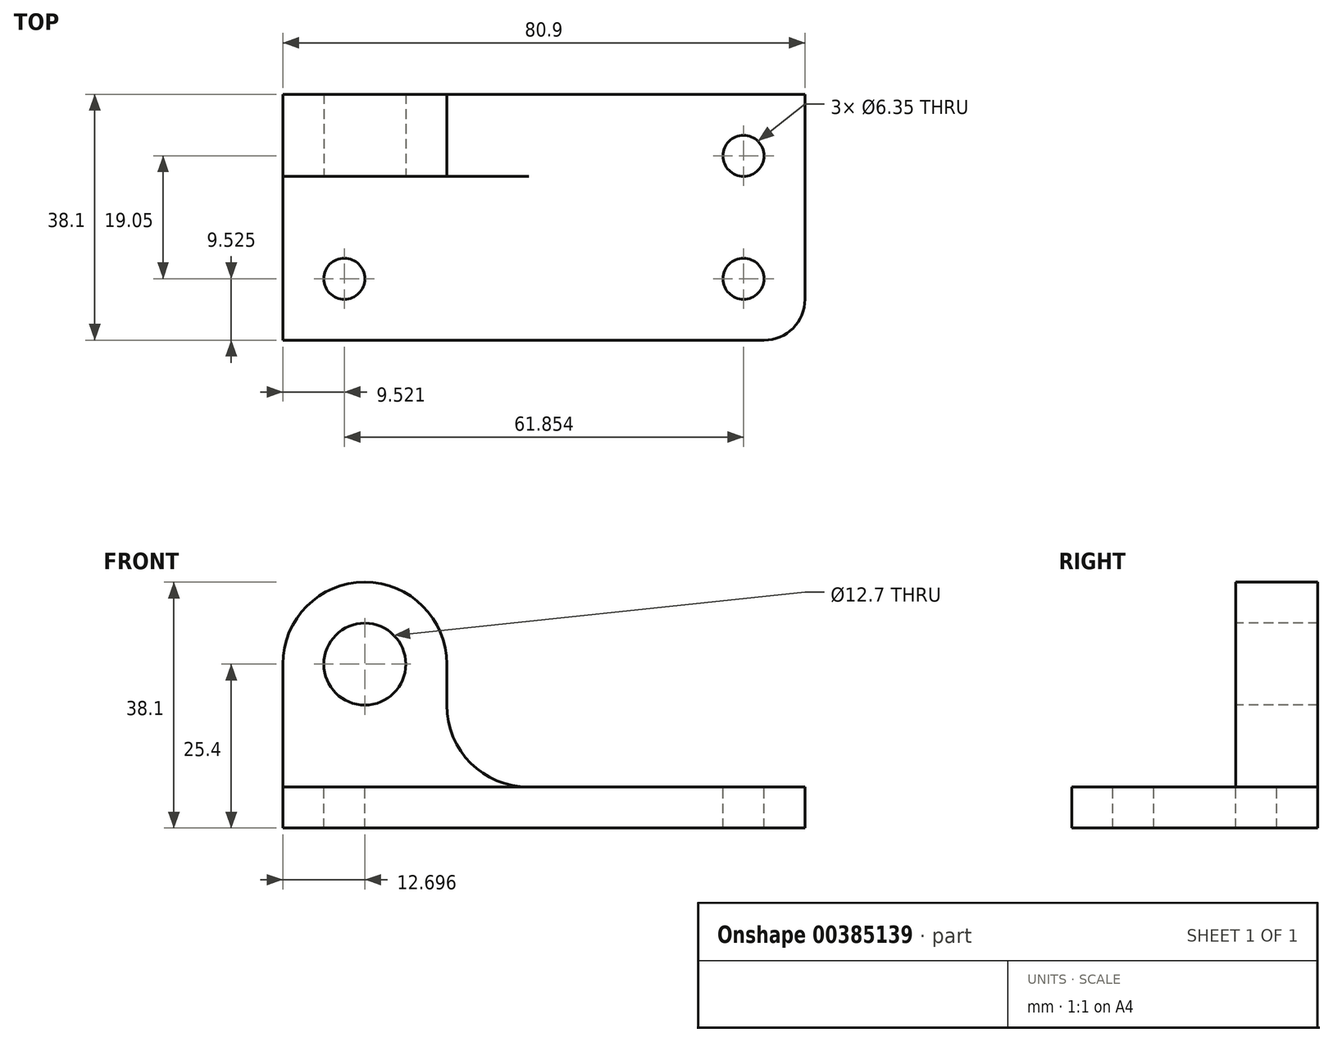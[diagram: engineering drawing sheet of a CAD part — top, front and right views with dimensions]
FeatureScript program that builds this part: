
annotation { "Feature Type Name" : "Feature", "Feature Type Description" : "" }
export const myFeature = defineFeature(function(context is Context, id is Id, definition is map)
    precondition{}
    {
        {
            var Q0;
            Q0=qCreatedBy(makeId("Front.planeOp"),FACE);
            var sketch = newSketch(context, id + "F0", { "sketchPlane" : qUnion([Q0])});
            skLineSegment(sketch, "E0", {"start": v(0, 0) * mm, "end": v(-80.9, 0) * mm});
            skLineSegment(sketch, "E1", {"start": v(-80.9, 0) * mm, "end": v(-80.9, 38.1) * mm});
            skLineSegment(sketch, "E2", {"start": v(-80.9, 38.1) * mm, "end": v(-55.5, 38.1) * mm});
            skLineSegment(sketch, "E3", {"start": v(-55.5, 38.1) * mm, "end": v(-55.5, 6.35) * mm});
            skLineSegment(sketch, "E4", {"start": v(-55.5, 6.35) * mm, "end": v(0, 6.35) * mm});
            skLineSegment(sketch, "E5", {"start": v(0, 6.35) * mm, "end": v(0, 0) * mm});
            skSolve(sketch);
        }
        {
            var Q0;
            Q0=makeQuery(id+"F0.imprint","IMPRINT",FACE,{"disambiguationData":[TD([[makeQuery(id+"F0.imprint","IMPRINT",EDGE,{"derivedFrom":sQuery(id+"F0.wireOp",EDGE,"E0")}),-1.0]])]});
            extrude(context, id + "F1", {"entities" : qUnion([Q0]), "depth" : 38.1 * mm});
        }
        {
            var Q0;
            Q0=makeQuery(id+"F1.opExtrude","SWEPT_FACE",FACE,{"disambiguationData":[OSD([sQuery(id+"F0.wireOp",EDGE,"E2")])]});
            var sketch = newSketch(context, id + "F2", { "sketchPlane" : qUnion([Q0])});
            skLineSegment(sketch, "E6", {"start": v(-80.9, -12.7) * mm, "end": v(-55.5, -12.7) * mm});
            skSolve(sketch);
        }
        {
            var Q0;
            {var subQ0=sQuery(id+"F2.wireOp",EDGE,"E6");Q0=makeQuery(id+"F2.imprint","IMPRINT",FACE,{"disambiguationData":[TD([[makeQuery(id+"F2.imprint","IMPRINT",EDGE,{"derivedFrom":subQ0}),-1.0]])]});}
            extrude(context, id + "F3", {"entities" : qUnion([Q0]), "operationType" : NewBodyOperationType.REMOVE, "oppositeDirection" : true, "depth" : 31.75 * mm});
        }
        {
            var Q0;
            Q0=makeQuery(id+"F3.boolean.opBoolean","MERGE",FACE,{"derivedFrom":[makeQuery(id+"F1.opExtrude","SWEPT_FACE",FACE,{"disambiguationData":[OSD([sQuery(id+"F0.wireOp",EDGE,"E4")])]}),makeQuery(id+"F3.opExtrude","CAP_FACE",FACE,{"disambiguationData":[OSD([sQuery(id+"F0.wireOp",EDGE,"E1"),sQuery(id+"F0.wireOp",EDGE,"E2"),sQuery(id+"F0.wireOp",EDGE,"E3"),sQuery(id+"F2.wireOp",EDGE,"E6")])],"isStart":false})]});
            var sketch = newSketch(context, id + "F4", { "sketchPlane" : qUnion([Q0])});
            skLineSegment(sketch, "E7", {"start": v(-55.5, 0) * mm, "end": v(-42.8, 0) * mm});
            skLineSegment(sketch, "E8", {"start": v(-55.5, -12.7) * mm, "end": v(-42.8, -12.7) * mm});
            skLineSegment(sketch, "E9", {"start": v(-42.8, 0) * mm, "end": v(-42.8, -12.7) * mm});
            skSolve(sketch);
        }
        {
            var Q0;
            Q0=makeQuery(id+"F4.imprint","IMPRINT",FACE,{"disambiguationData":[TD([[makeQuery(id+"F4.imprint","IMPRINT",EDGE,{"derivedFrom":sQuery(id+"F4.wireOp",EDGE,"E7")}),-1.0]])]});
            extrude(context, id + "F5", {"entities" : qUnion([Q0]), "operationType" : NewBodyOperationType.ADD, "depth" : 12.7 * mm});
        }
        {
            var Q0;
            Q0=makeQuery(id+"F5.boolean.opBoolean","MERGE",FACE,{"derivedFrom":[makeQuery(id+"F1.opExtrude","CAP_FACE",FACE,{"disambiguationData":[OSD([sQuery(id+"F0.wireOp",EDGE,"E0"),sQuery(id+"F0.wireOp",EDGE,"E1"),sQuery(id+"F0.wireOp",EDGE,"E2"),sQuery(id+"F0.wireOp",EDGE,"E3"),sQuery(id+"F0.wireOp",EDGE,"E4"),sQuery(id+"F0.wireOp",EDGE,"E5")])],"isStart":true}),makeQuery(id+"F5.opExtrude","SWEPT_FACE",FACE,{"disambiguationData":[OSD([sQuery(id+"F4.wireOp",EDGE,"E7")])]})]});
            var sketch = newSketch(context, id + "F6", { "sketchPlane" : qUnion([Q0])});
            skCircle(sketch, "E10", {"center": v(42.8, 19.05) * mm, "radius": 12.7 * mm});
            skSolve(sketch);
        }
        {
            var Q0;
            {var subQ1=sQuery(id+"F4.wireOp",EDGE,"E7");var subQ2=makeQuery(id+"F5.opExtrude","CAP_EDGE",EDGE,{"disambiguationData":[OSD([subQ1])],"isStart":false});Q0=makeQuery(id+"F6.imprint","IMPRINT",FACE,{"disambiguationData":[TD([[makeQuery(id+"F6.imprint","IMPRINT",EDGE,{"derivedFrom":subQ2}),1.0]])]});}
            extrude(context, id + "F7", {"entities" : qUnion([Q0]), "operationType" : NewBodyOperationType.REMOVE, "oppositeDirection" : true, "depth" : 25.4 * mm});
        }
        {
            var Q0;
            Q0=makeQuery(id+"F5.boolean.opBoolean","MERGE",FACE,{"derivedFrom":[makeQuery(id+"F3.boolean.opBoolean","COPY",FACE,{"derivedFrom":makeQuery(id+"F3.opExtrude","SWEPT_FACE",FACE,{"disambiguationData":[OSD([sQuery(id+"F2.wireOp",EDGE,"E6")])]})}),makeQuery(id+"F5.opExtrude","SWEPT_FACE",FACE,{"disambiguationData":[OSD([sQuery(id+"F4.wireOp",EDGE,"E8")])]})]});
            var sketch = newSketch(context, id + "F8", { "sketchPlane" : qUnion([Q0])});
            skCircle(sketch, "E11", {"center": v(-68.2, 25.4) * mm, "radius": 12.7 * mm});
            skSolve(sketch);
        }
        {
            var Q0;
            {var subQ0=sQuery(id+"F8.wireOp",EDGE,"E11");var subQ1=sQuery(id+"F2.wireOp",EDGE,"E6");var subQ2=makeQuery(id+"F3.boolean.opBoolean","COPY",EDGE,{"derivedFrom":makeQuery(id+"F3.opExtrude","CAP_EDGE",EDGE,{"disambiguationData":[OSD([subQ1])],"isStart":true})});var subQ3=makeQuery(id+"F8.imprint","INTERSECT",VERTEX,{"derivedFrom":[subQ2,subQ0]});Q0=makeQuery(id+"F8.imprint","IMPRINT",FACE,{"disambiguationData":[TD([[makeQuery(id+"F8.imprint","IMPRINT",EDGE,{"disambiguationData":[TD([[subQ3,-1.0]])],"derivedFrom":subQ0}),-1.0]])]});}
            var Q1;
            {var subQ0=sQuery(id+"F8.wireOp",EDGE,"E11");var subQ1=sQuery(id+"F2.wireOp",EDGE,"E6");var subQ2=makeQuery(id+"F3.boolean.opBoolean","COPY",EDGE,{"derivedFrom":makeQuery(id+"F3.opExtrude","CAP_EDGE",EDGE,{"disambiguationData":[OSD([subQ1])],"isStart":true})});var subQ3=makeQuery(id+"F8.imprint","INTERSECT",VERTEX,{"derivedFrom":[subQ2,subQ0]});Q1=makeQuery(id+"F8.imprint","IMPRINT",FACE,{"disambiguationData":[TD([[makeQuery(id+"F8.imprint","IMPRINT",EDGE,{"disambiguationData":[TD([[subQ3,1.0]])],"derivedFrom":subQ0}),-1.0]])]});}
            extrude(context, id + "F9", {"entities" : qUnion([Q0, Q1]), "operationType" : NewBodyOperationType.REMOVE, "oppositeDirection" : true, "depth" : 25.4 * mm});
        }
        {
            var Q0;
            Q0=makeQuery(id+"F5.boolean.opBoolean","MERGE",FACE,{"derivedFrom":[makeQuery(id+"F3.boolean.opBoolean","COPY",FACE,{"derivedFrom":makeQuery(id+"F3.opExtrude","SWEPT_FACE",FACE,{"disambiguationData":[OSD([sQuery(id+"F2.wireOp",EDGE,"E6")])]})}),makeQuery(id+"F5.opExtrude","SWEPT_FACE",FACE,{"disambiguationData":[OSD([sQuery(id+"F4.wireOp",EDGE,"E8")])]})]});
            var sketch = newSketch(context, id + "F10", { "sketchPlane" : qUnion([Q0])});
            skCircle(sketch, "E12", {"center": v(-68.2, 25.4) * mm, "radius": 6.35 * mm});
            skSolve(sketch);
        }
        {
            var Q0;
            Q0=makeQuery(id+"F10.imprint","IMPRINT",FACE,{"disambiguationData":[TD([[makeQuery(id+"F10.imprint","IMPRINT",EDGE,{"derivedFrom":sQuery(id+"F10.wireOp",EDGE,"E12")}),1.0]])]});
            extrude(context, id + "F11", {"entities" : qUnion([Q0]), "operationType" : NewBodyOperationType.REMOVE, "oppositeDirection" : true, "depth" : 25.4 * mm});
        }
        {
            var Q0;
            Q0=makeQuery(id+"F3.boolean.opBoolean","MERGE",FACE,{"derivedFrom":[makeQuery(id+"F1.opExtrude","SWEPT_FACE",FACE,{"disambiguationData":[OSD([sQuery(id+"F0.wireOp",EDGE,"E4")])]}),makeQuery(id+"F3.opExtrude","CAP_FACE",FACE,{"disambiguationData":[OSD([sQuery(id+"F0.wireOp",EDGE,"E1"),sQuery(id+"F0.wireOp",EDGE,"E2"),sQuery(id+"F0.wireOp",EDGE,"E3"),sQuery(id+"F2.wireOp",EDGE,"E6")])],"isStart":false})]});
            var sketch = newSketch(context, id + "F12", { "sketchPlane" : qUnion([Q0])});
            skCircle(sketch, "E13", {"center": v(-9.52, -9.52) * mm, "radius": 3.18 * mm});
            skCircle(sketch, "E14", {"center": v(-9.52, -28.58) * mm, "radius": 3.18 * mm});
            skCircle(sketch, "E15", {"center": v(-71.38, -28.58) * mm, "radius": 3.18 * mm});
            skSolve(sketch);
        }
        {
            var Q0;
            Q0=makeQuery(id+"F12.imprint","IMPRINT",FACE,{"disambiguationData":[TD([[makeQuery(id+"F12.imprint","IMPRINT",EDGE,{"derivedFrom":sQuery(id+"F12.wireOp",EDGE,"E13")}),1.0]])]});
            var Q1;
            Q1=makeQuery(id+"F12.imprint","IMPRINT",FACE,{"disambiguationData":[TD([[makeQuery(id+"F12.imprint","IMPRINT",EDGE,{"derivedFrom":sQuery(id+"F12.wireOp",EDGE,"E14")}),1.0]])]});
            var Q2;
            Q2=makeQuery(id+"F12.imprint","IMPRINT",FACE,{"disambiguationData":[TD([[makeQuery(id+"F12.imprint","IMPRINT",EDGE,{"derivedFrom":sQuery(id+"F12.wireOp",EDGE,"E15")}),1.0]])]});
            extrude(context, id + "F13", {"entities" : qUnion([Q0, Q1, Q2]), "operationType" : NewBodyOperationType.REMOVE, "oppositeDirection" : true, "depth" : 25.4 * mm});
        }
        {
            var Q0;
            Q0=makeQuery(id+"F3.boolean.opBoolean","MERGE",FACE,{"derivedFrom":[makeQuery(id+"F1.opExtrude","SWEPT_FACE",FACE,{"disambiguationData":[OSD([sQuery(id+"F0.wireOp",EDGE,"E4")])]}),makeQuery(id+"F3.opExtrude","CAP_FACE",FACE,{"disambiguationData":[OSD([sQuery(id+"F0.wireOp",EDGE,"E1"),sQuery(id+"F0.wireOp",EDGE,"E2"),sQuery(id+"F0.wireOp",EDGE,"E3"),sQuery(id+"F2.wireOp",EDGE,"E6")])],"isStart":false})]});
            var sketch = newSketch(context, id + "F14", { "sketchPlane" : qUnion([Q0])});
            skCircle(sketch, "E16", {"center": v(-74.55, -31.75) * mm, "radius": 6.35 * mm});
            skCircle(sketch, "E17", {"center": v(-6.35, -31.75) * mm, "radius": 6.35 * mm});
            skSolve(sketch);
        }
        {
            var Q0;
            {var subQ0=sQuery(id+"F14.wireOp",EDGE,"E16");var subQ1=sQuery(id+"F0.wireOp",EDGE,"E2");var subQ2=makeQuery(id+"F3.boolean.opBoolean","COPY",EDGE,{"derivedFrom":makeQuery(id+"F3.opExtrude","CAP_EDGE",EDGE,{"disambiguationData":[OSD([sQuery(id+"F0.wireOp",EDGE,"E1"),subQ1])],"isStart":false})});var subQ3=makeQuery(id+"F14.imprint","INTERSECT",VERTEX,{"derivedFrom":[subQ2,subQ0]});Q0=makeQuery(id+"F14.imprint","IMPRINT",FACE,{"disambiguationData":[TD([[makeQuery(id+"F14.imprint","IMPRINT",EDGE,{"disambiguationData":[TD([[subQ3,-1.0]])],"derivedFrom":subQ0}),-1.0]])]});}
            var Q1;
            {var subQ0=sQuery(id+"F14.wireOp",EDGE,"E17");var subQ1=sQuery(id+"F0.wireOp",EDGE,"E4");var subQ2=makeQuery(id+"F1.opExtrude","SWEPT_EDGE",EDGE,{"disambiguationData":[OSD([subQ1,sQuery(id+"F0.wireOp",EDGE,"E5")])]});var subQ3=makeQuery(id+"F14.imprint","INTERSECT",VERTEX,{"derivedFrom":[subQ2,subQ0]});Q1=makeQuery(id+"F14.imprint","IMPRINT",FACE,{"disambiguationData":[TD([[makeQuery(id+"F14.imprint","IMPRINT",EDGE,{"disambiguationData":[TD([[subQ3,1.0]])],"derivedFrom":subQ0}),-1.0]])]});}
            extrude(context, id + "F15", {"entities" : qUnion([Q0, Q1]), "operationType" : NewBodyOperationType.REMOVE, "oppositeDirection" : true, "depth" : 25.4 * mm});
        }
    });
